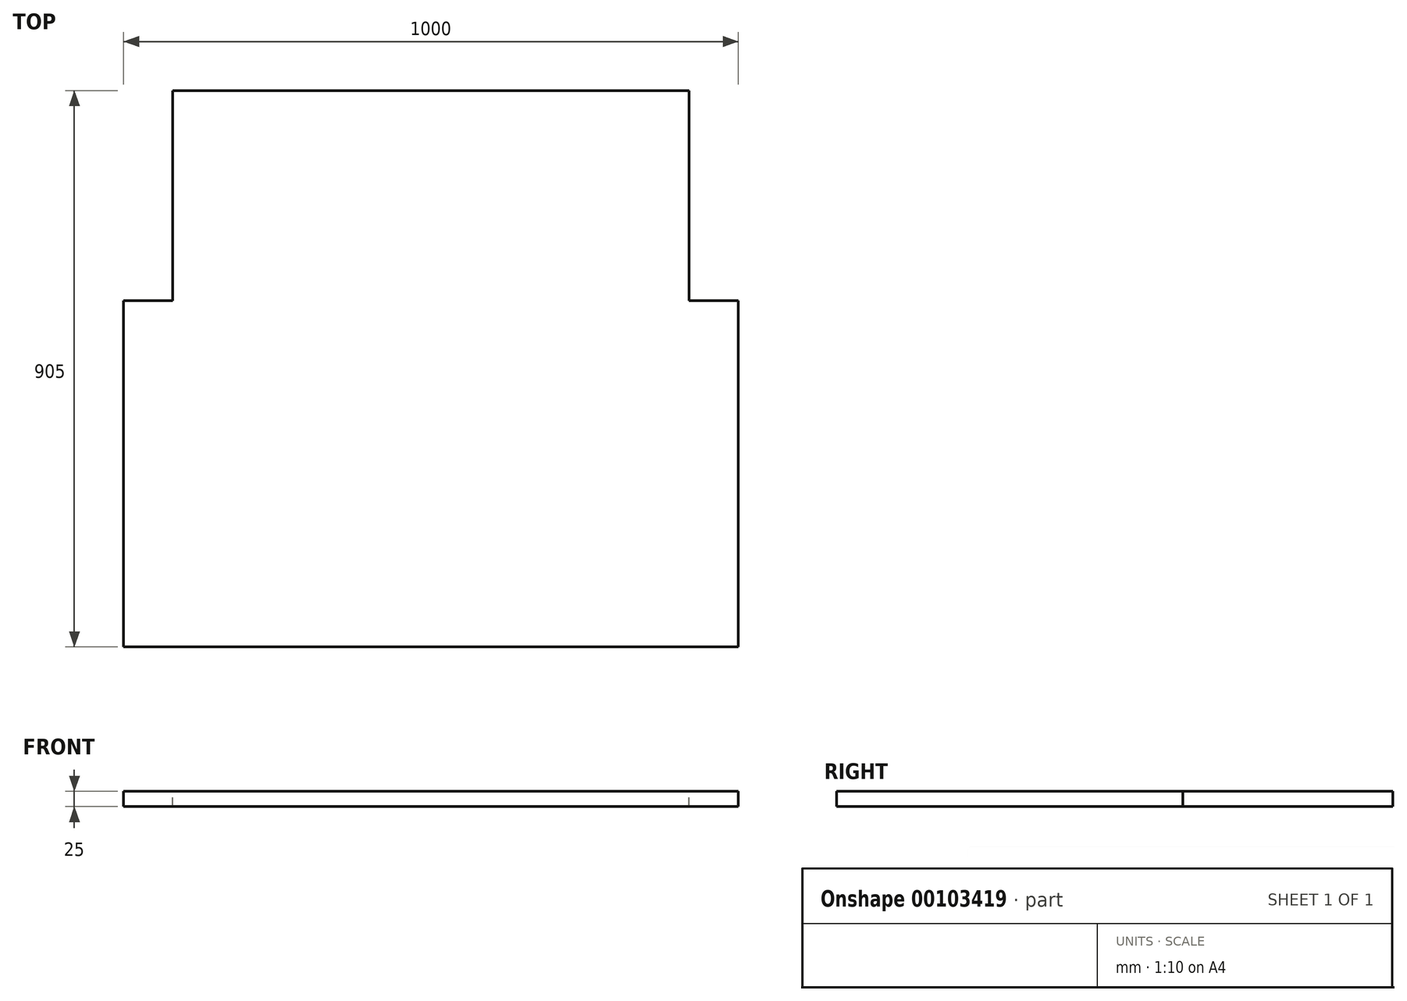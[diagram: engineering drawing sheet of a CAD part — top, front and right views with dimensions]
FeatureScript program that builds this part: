
annotation { "Feature Type Name" : "Feature", "Feature Type Description" : "" }
export const myFeature = defineFeature(function(context is Context, id is Id, definition is map)
    precondition{}
    {
        {
            var Q0;
            Q0=qCreatedBy(makeId("Top.planeOp"),FACE);
            var sketch = newSketch(context, id + "F0", { "sketchPlane" : qUnion([Q0])});
            skLineSegment(sketch, "E0.bottom", {"start": v(-500, 0) * mm, "end": v(500, 0) * mm});
            skLineSegment(sketch, "E0.top", {"start": v(-500, 905) * mm, "end": v(500, 905) * mm});
            skLineSegment(sketch, "E0.left", {"start": v(-500, 0) * mm, "end": v(-500, 905) * mm});
            skLineSegment(sketch, "E0.right", {"start": v(500, 0) * mm, "end": v(500, 905) * mm});
            skSolve(sketch);
        }
        {
            var Q0;
            Q0 = qSketchRegion(id + "F0", true);
            extrude(context, id + "F1", {"entities" : qUnion([Q0]), "oppositeDirection" : true, "depth" : 25 * mm, "offsetDistance" : 25 * mm});
        }
        {
            var Q0;
            Q0=makeQuery(id+"F1.opExtrude","CAP_FACE",FACE,{"disambiguationData":[OSD([sQuery(id+"F0.wireOp",EDGE,"E0.bottom"),sQuery(id+"F0.wireOp",EDGE,"E0.top"),sQuery(id+"F0.wireOp",EDGE,"E0.left"),sQuery(id+"F0.wireOp",EDGE,"E0.right")])],"isStart":true});
            var sketch = newSketch(context, id + "F2", { "sketchPlane" : qUnion([Q0])});
            skLineSegment(sketch, "E1.0", {"start": v(-420, 563) * mm, "end": v(-500, 563) * mm});
            skLineSegment(sketch, "E2.0", {"start": v(-420, 1134.7) * mm, "end": v(-420, 563) * mm});
            skLineSegment(sketch, "E3.0", {"start": v(420, 1134.7) * mm, "end": v(420, 563) * mm});
            skLineSegment(sketch, "E4.0", {"start": v(420, 563) * mm, "end": v(500, 563) * mm});
            skSolve(sketch);
        }
        {
            var Q0;
            {var subQ0=sQuery(id+"F2.wireOp",EDGE,"E2.0");var subQ1=sQuery(id+"F2.wireOp",EDGE,"E1.0");var subQ2=makeQuery(id+"F2.imprint","INTERSECT",VERTEX,{"derivedFrom":[subQ1,subQ0]});Q0=makeQuery(id+"F2.imprint","IMPRINT",FACE,{"disambiguationData":[TD([[makeQuery(id+"F2.imprint","IMPRINT",EDGE,{"disambiguationData":[TD([[subQ2,-1.0]])],"derivedFrom":subQ1}),-1.0]])]});}
            var Q1;
            {var subQ0=sQuery(id+"F2.wireOp",EDGE,"E4.0");var subQ1=sQuery(id+"F2.wireOp",EDGE,"E3.0");var subQ2=makeQuery(id+"F2.imprint","INTERSECT",VERTEX,{"derivedFrom":[subQ1,subQ0]});Q1=makeQuery(id+"F2.imprint","IMPRINT",FACE,{"disambiguationData":[TD([[makeQuery(id+"F2.imprint","IMPRINT",EDGE,{"disambiguationData":[TD([[subQ2,1.0]])],"derivedFrom":subQ1}),1.0]])]});}
            extrude(context, id + "F3", {"entities" : qUnion([Q0, Q1]), "operationType" : NewBodyOperationType.REMOVE, "oppositeDirection" : true, "depth" : 25 * mm, "offsetDistance" : 25 * mm});
        }
    });
